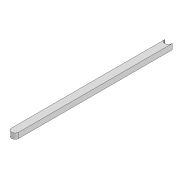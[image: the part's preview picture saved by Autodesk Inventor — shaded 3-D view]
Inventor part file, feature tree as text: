
AUTODESK INVENTOR PART (.ipt)
format: ipt  version: 2022 (Build 260153000, 153)  size: 80,896 bytes
history: native  units: mm
features: extrude x1, sketch x1
ambient origin geometry x8: Origin, YZ Plane, XZ Plane, XY Plane, X Axis, Y Axis, Z Axis, Center Point
bodies: Solid1 (feature_tree)
feature tree (2):
  extrude  "Extrusion1"  Depth=8.0mm
  sketch  "Sketch1"  dims[d0=170.0mm d1=8.0mm d2=6.0mm d3=0.0mm]
